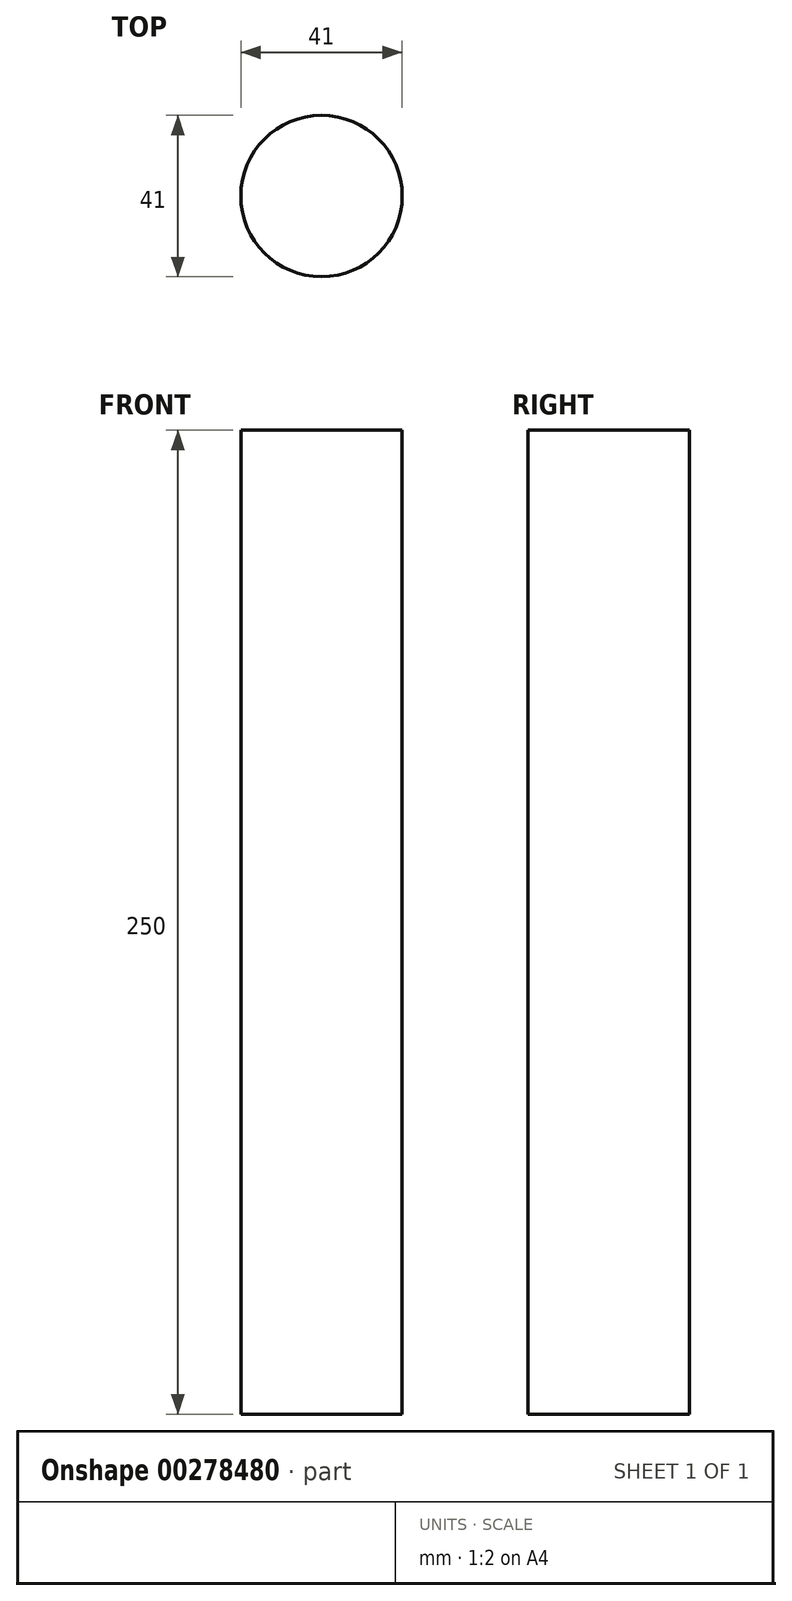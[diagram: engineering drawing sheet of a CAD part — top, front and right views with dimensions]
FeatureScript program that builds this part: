
annotation { "Feature Type Name" : "Feature", "Feature Type Description" : "" }
export const myFeature = defineFeature(function(context is Context, id is Id, definition is map)
    precondition{}
    {
        {
            var Q0;
            Q0=qCreatedBy(makeId("Top.planeOp"),FACE);
            var sketch = newSketch(context, id + "F0", { "sketchPlane" : qUnion([Q0])});
            skCircle(sketch, "E0", {"center": v(0, 0) * mm, "radius": 20.5 * mm});
            skSolve(sketch);
        }
        {
            var Q0;
            Q0 = qSketchRegion(id + "F0", true);
            extrude(context, id + "F1", {"entities" : qUnion([Q0]), "depth" : 250 * mm});
        }
    });
